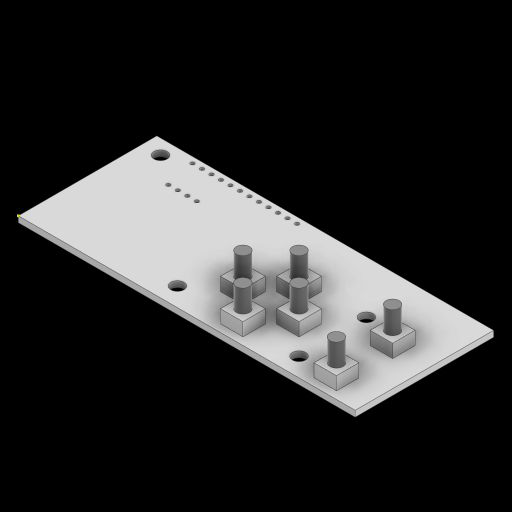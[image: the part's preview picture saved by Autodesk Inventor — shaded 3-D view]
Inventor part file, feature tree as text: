
AUTODESK INVENTOR PART (.ipt)
format: ipt  version: 2024 (Build 280153000, 153)  size: 287,232 bytes
history: native  units: mm
features: sketch x7, extrude x6, projected_geometry x6, pattern_linear x1
ambient origin geometry x8: Origin, YZ Plane, XZ Plane, XY Plane, X Axis, Y Axis, Z Axis, Center Point
bodies: Volumenkörper1 (feature_tree)
feature tree (20):
  extrude  "Extrusion1"  Depth=37.0mm
  extrude  "Extrusion2"  Depth=3.5mm
  extrude  "Extrusion3"  Depth=3.5mm
  pattern_linear  "Rechteckige Anordnung1"  Spacing1=5.0mm  [1 undecoded]
  extrude  "Extrusion4"  Depth=6.0mm
  extrude  "Extrusion5"  Depth=6.0mm
  extrude  "Buttons"  Depth=6.0mm
  sketch  "Skizze7"  dims[d10=37.5mm d11=5.0mm d12=5.0mm d14=70.0mm d15=70.0mm d16=23.0mm d17=1.6mm d18=0.0mm d19=1.0mm d20=35.373mm d21=11.152mm d22=1.0mm d23=27.192mm d24=12.889mm d25=1.6mm d26=0.0mm d27=120.0mm d29=2.54mm d30=1.0mm d31=1.0mm d32=1.0mm d33=1.0mm d34=1.6mm d35=0.0mm d53=6.0mm d54=6.0mm d55=12.5mm d56=47.5mm d57=6.0mm d58=6.0mm d59=55.0mm d60=20.0mm d61=6.0mm d62=6.0mm d63=5.0mm d64=55.0mm d65=6.0mm d66=6.0mm d67=62.5mm d68=12.5mm d69=6.0mm d70=6.0mm d71=20.0mm d72=80.0mm d73=6.0mm d74=6.0mm d75=5.0mm d76=80.0mm d77=3.5mm d78=0.0mm d79=3.5mm d80=3.5mm d81=3.5mm d82=3.5mm d83=3.5mm d84=3.5mm d85=6.0mm d86=0.0mm]
  sketch  "Skizze1"  dims[d0=90.0mm d1=37.0mm]
  sketch  "Skizze2"  dims[d2=1.6mm d3=0.0mm d4=3.5mm]
  sketch  "Skizze3"  dims[d5=3.5mm d6=3.5mm]
  sketch  "Skizze4"  dims[d7=3.5mm]
  sketch  "Skizze5"  dims[d8=33.0mm]
  sketch  "Skizze6"  dims[d9=5.0mm]
  projected_geometry  "Projizierte Kontur1"
  projected_geometry  "Projizierte Kontur2"
  projected_geometry  "Projizierte Kontur3"
  projected_geometry  "Projizierte Kontur4"
  projected_geometry  "Projizierte Kontur5"
  projected_geometry  "Projizierte Kontur6"
note: 1 required parameter value undecoded (feature->parameter linkage not recoverable at this tier; creation-order binding heuristic only, values carry confidence <= 0.55)
